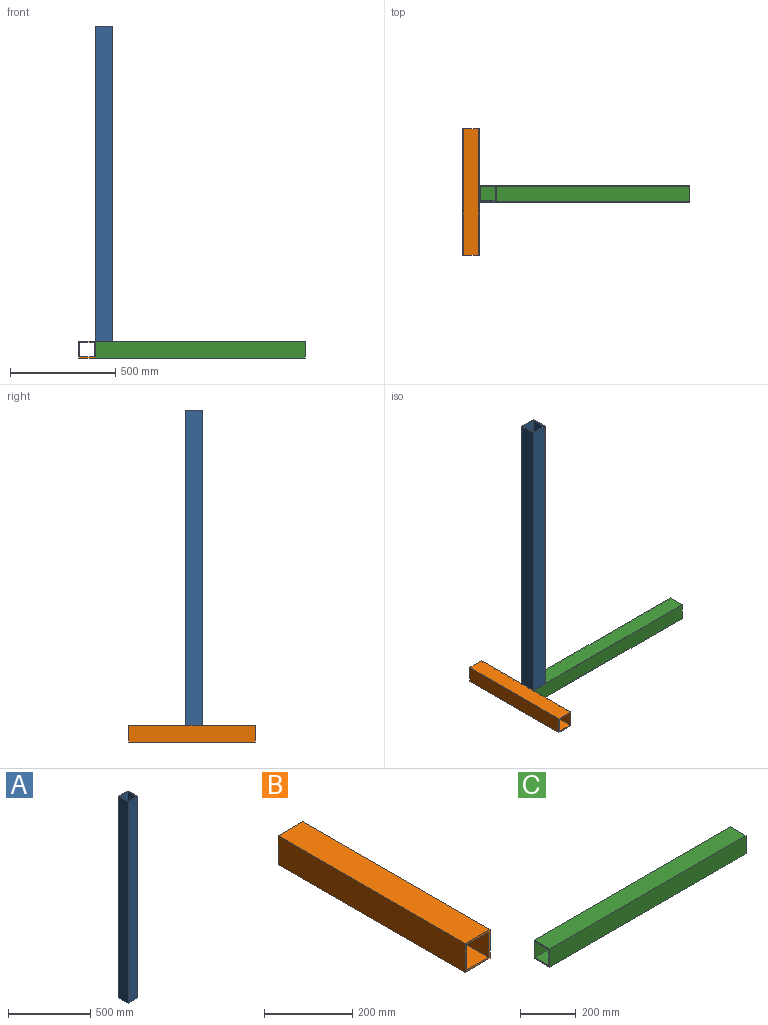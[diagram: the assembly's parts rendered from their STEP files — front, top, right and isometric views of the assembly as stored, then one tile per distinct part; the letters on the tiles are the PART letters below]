
ASSEMBLY  parts=3 mates=5
PART A: 10 faces, bbox 80x80x1500 mm
  f0: plane 1500x70mm, normal (-1,0,0), area 105000mm2, adj f1,f7,f8,f9
  f1: plane 1500x70mm, normal (0,1,0), area 105000mm2, adj f0,f2,f8,f9
  f2: plane 1500x70mm, normal (1,0,0), area 105000mm2, adj f1,f7,f8,f9
  f3: plane 1500x80mm, normal (-1,0,0), area 120000mm2, adj f4,f6,f8,f9
  f4: plane 1500x80mm, normal (0,-1,0), area 120000mm2, adj f3,f5,f8,f9
  f5: plane 1500x80mm, normal (1,0,0), area 120000mm2, adj f4,f6,f8,f9
  f6: plane 1500x80mm, normal (0,1,0), area 120000mm2, adj f3,f5,f8,f9
  f7: plane 1500x70mm, normal (0,-1,0), area 105000mm2, adj f0,f2,f8,f9
  f8: plane 80x80mm, normal (0,0,1), area 1500mm2, adj f0,f1,f2,f3,f4,f5,f6,f7
  f9: plane 80x80mm, normal (0,0,-1), area 1500mm2, adj f0,f1,f2,f3,f4,f5,f6,f7
PART B: 10 faces, bbox 80x600x80 mm
  f0: plane 600x70mm, normal (-1,0,0), area 42000mm2, adj f1,f7,f8,f9
  f1: plane 600x70mm, normal (0,0,1), area 42000mm2, adj f0,f2,f8,f9
  f2: plane 600x70mm, normal (1,0,0), area 42000mm2, adj f1,f7,f8,f9
  f3: plane 600x80mm, normal (-1,0,0), area 48000mm2, adj f4,f6,f8,f9
  f4: plane 600x80mm, normal (0,0,-1), area 48000mm2, adj f3,f5,f8,f9
  f5: plane 600x80mm, normal (1,0,0), area 48000mm2, adj f4,f6,f8,f9
  f6: plane 600x80mm, normal (0,0,1), area 48000mm2, adj f3,f5,f8,f9
  f7: plane 600x70mm, normal (0,0,-1), area 42000mm2, adj f0,f2,f8,f9
  f8: plane 80x80mm, normal (0,-1,0), area 1500mm2, adj f0,f1,f2,f3,f4,f5,f6,f7
  f9: plane 80x80mm, normal (0,1,0), area 1500mm2, adj f0,f1,f2,f3,f4,f5,f6,f7
PART C: 10 faces, bbox 1000x80x80 mm
  f0: plane 1000x80mm, normal (0,0,-1), area 80000mm2, adj f1,f7,f8,f9
  f1: plane 1000x80mm, normal (0,1,0), area 80000mm2, adj f0,f2,f8,f9
  f2: plane 1000x80mm, normal (0,0,1), area 80000mm2, adj f1,f7,f8,f9
  f3: plane 1000x70mm, normal (0,0,1), area 70000mm2, adj f4,f6,f8,f9
  f4: plane 1000x70mm, normal (0,1,0), area 70000mm2, adj f3,f5,f8,f9
  f5: plane 1000x70mm, normal (0,0,-1), area 70000mm2, adj f4,f6,f8,f9
  f6: plane 1000x70mm, normal (0,-1,0), area 70000mm2, adj f3,f5,f8,f9
  f7: plane 1000x80mm, normal (0,-1,0), area 80000mm2, adj f0,f2,f8,f9
  f8: plane 80x80mm, normal (1,0,0), area 1500mm2, adj f0,f1,f2,f3,f4,f5,f6,f7
  f9: plane 80x80mm, normal (-1,0,0), area 1500mm2, adj f0,f1,f2,f3,f4,f5,f6,f7
PLACE A t=(-499.5,-177.93,968.41)mm
PLACE B t=(-579.5,-168.38,178.41)mm
PLACE C t=(-39.5,-177.93,178.41)mm fixed
MATE planar B.f6 <-> C.f2  axis (0,0,1) through (-619.5,131.62,218.41)mm
MATE planar C.f7 <-> A.f4  axis (0,-1,0) through (-39.5,-217.93,178.41)mm
MATE planar B.f5 <-> C.f9  axis (1,0,0) through (-539.5,-168.38,218.41)mm
MATE planar A.f3 <-> C.f9  axis (-1,0,0) through (-539.5,-177.93,968.41)mm
MATE planar A.f9 <-> C.f2  axis (0,0,-1) through (-534.5,-212.93,218.41)mm
